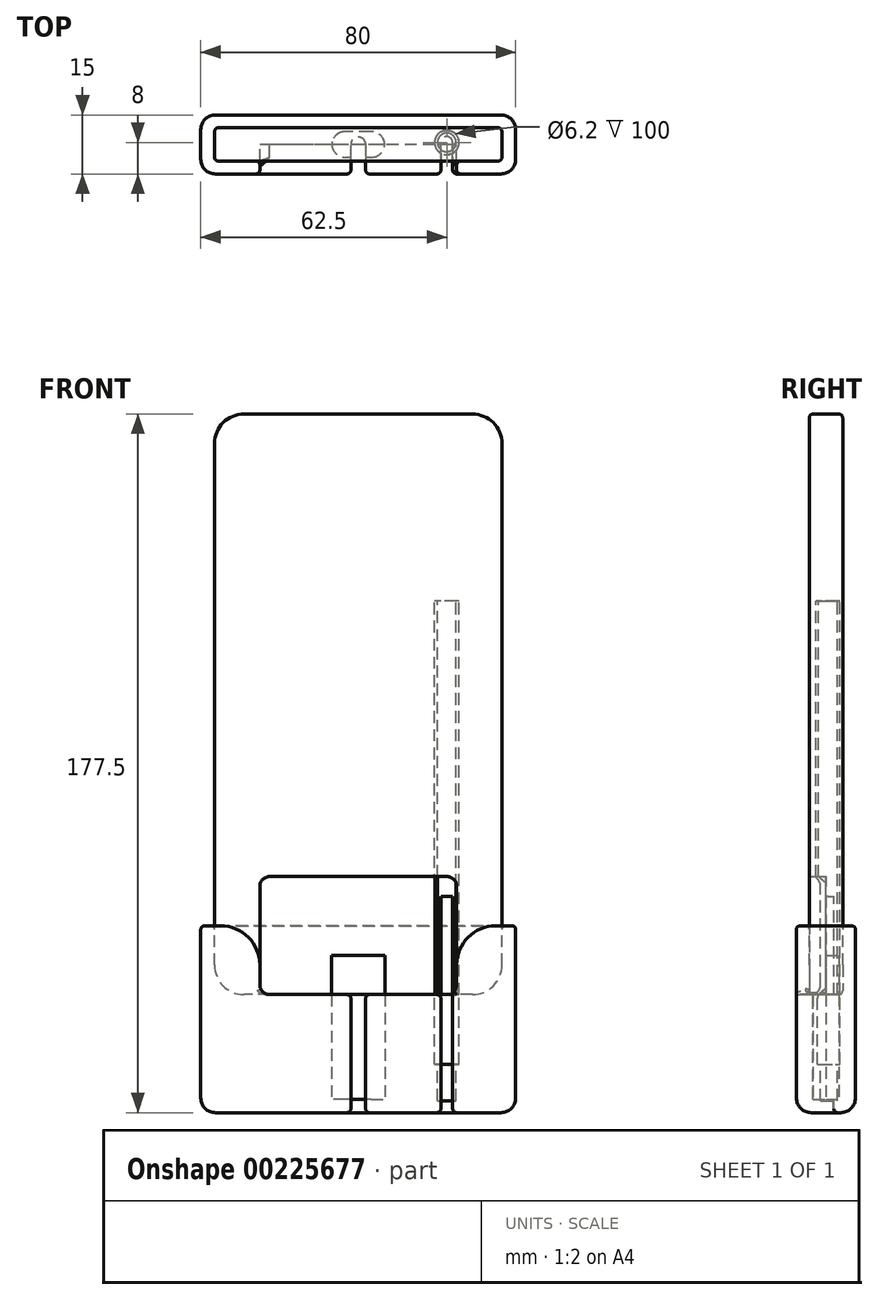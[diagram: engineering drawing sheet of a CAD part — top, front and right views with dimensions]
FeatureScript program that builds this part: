
annotation { "Feature Type Name" : "Feature", "Feature Type Description" : "" }
export const myFeature = defineFeature(function(context is Context, id is Id, definition is map)
    precondition{}
    {
        {
            var Q0;
            Q0=qCreatedBy(makeId("Front.planeOp"),FACE);
            var sketch = newSketch(context, id + "F0", { "sketchPlane" : qUnion([Q0])});
            skLineSegment(sketch, "E0.bottom", {"start": v(29, 0) * mm, "end": v(-29, 0) * mm});
            skLineSegment(sketch, "E0.top", {"start": v(29, 147.5) * mm, "end": v(-29, 147.5) * mm});
            skLineSegment(sketch, "E0.left", {"start": v(36.5, 7.5) * mm, "end": v(36.5, 140) * mm});
            skLineSegment(sketch, "E0.right", {"start": v(-36.5, 7.5) * mm, "end": v(-36.5, 140) * mm});
            skPoint(sketch, "E1.visualSharp", {"position": v(36.5, 147.5) * mm});
            skArc(sketch, "E1.filletArc", {"start": v(36.5, 140) * mm, "mid": v(34.3, 145.3) * mm, "end": v(29, 147.5) * mm});
            skPoint(sketch, "E2.visualSharp", {"position": v(-36.5, 147.5) * mm});
            skArc(sketch, "E2.filletArc", {"start": v(-29, 147.5) * mm, "mid": v(-34.3, 145.3) * mm, "end": v(-36.5, 140) * mm});
            skPoint(sketch, "E3.visualSharp", {"position": v(36.5, 0) * mm});
            skArc(sketch, "E3.filletArc", {"start": v(29, 0) * mm, "mid": v(34.3, 2.2) * mm, "end": v(36.5, 7.5) * mm});
            skPoint(sketch, "E4.visualSharp", {"position": v(-36.5, 0) * mm});
            skArc(sketch, "E4.filletArc", {"start": v(-36.5, 7.5) * mm, "mid": v(-34.3, 2.2) * mm, "end": v(-29, 0) * mm});
            skSolve(sketch);
        }
        {
            var Q0;
            Q0=makeQuery(id+"F0.imprint","IMPRINT",FACE,{"disambiguationData":[TD([[makeQuery(id+"F0.imprint","IMPRINT",EDGE,{"derivedFrom":sQuery(id+"F0.wireOp",EDGE,"E0.bottom")}),-1.0]])]});
            extrude(context, id + "F1", {"entities" : qUnion([Q0]), "endBound" : BoundingType.SYMMETRIC, "depth" : 8.5 * mm});
        }
        {
            var Q0;
            Q0=makeQuery(id+"F1.opExtrude","CAP_FACE",FACE,{"disambiguationData":[OSD([sQuery(id+"F0.wireOp",EDGE,"E0.bottom"),sQuery(id+"F0.wireOp",EDGE,"E0.top"),sQuery(id+"F0.wireOp",EDGE,"E0.left"),sQuery(id+"F0.wireOp",EDGE,"E0.right"),sQuery(id+"F0.wireOp",EDGE,"E1.filletArc"),sQuery(id+"F0.wireOp",EDGE,"E2.filletArc"),sQuery(id+"F0.wireOp",EDGE,"E3.filletArc"),sQuery(id+"F0.wireOp",EDGE,"E4.filletArc")])],"isStart":false});
            var Q1;
            Q1=makeQuery(id+"F1.opExtrude","CAP_FACE",FACE,{"disambiguationData":[OSD([sQuery(id+"F0.wireOp",EDGE,"E0.bottom"),sQuery(id+"F0.wireOp",EDGE,"E0.top"),sQuery(id+"F0.wireOp",EDGE,"E0.left"),sQuery(id+"F0.wireOp",EDGE,"E0.right"),sQuery(id+"F0.wireOp",EDGE,"E1.filletArc"),sQuery(id+"F0.wireOp",EDGE,"E2.filletArc"),sQuery(id+"F0.wireOp",EDGE,"E3.filletArc"),sQuery(id+"F0.wireOp",EDGE,"E4.filletArc")])],"isStart":true});
            fillet(context, id + "F2", {"entities" : qUnion([Q0, Q1]), "radius" : 1 * mm, "tangentPropagation" : true, "allowEdgeOverflow" : false});
        }
        {
            var Q0;
            Q0=qCreatedBy(makeId("Top.planeOp"),FACE);
            var sketch = newSketch(context, id + "F3", { "sketchPlane" : qUnion([Q0])});
            skLineSegment(sketch, "E5.bottom", {"start": v(36.25, -7.5) * mm, "end": v(-36.25, -7.5) * mm});
            skLineSegment(sketch, "E5.top", {"start": v(36.25, 7.5) * mm, "end": v(-36.25, 7.5) * mm});
            skLineSegment(sketch, "E5.left", {"start": v(40, -3.75) * mm, "end": v(40, 3.75) * mm});
            skLineSegment(sketch, "E5.right", {"start": v(-40, -3.75) * mm, "end": v(-40, 3.75) * mm});
            skPoint(sketch, "E5.middle", {"position": v(0, 0) * mm});
            skPoint(sketch, "E6.visualSharp", {"position": v(-40, 7.5) * mm});
            skArc(sketch, "E6.filletArc", {"start": v(-36.25, 7.5) * mm, "mid": v(-38.9, 6.4) * mm, "end": v(-40, 3.75) * mm});
            skPoint(sketch, "E7.visualSharp", {"position": v(-40, -7.5) * mm});
            skArc(sketch, "E7.filletArc", {"start": v(-40, -3.75) * mm, "mid": v(-38.9, -6.4) * mm, "end": v(-36.25, -7.5) * mm});
            skPoint(sketch, "E8.visualSharp", {"position": v(40, 7.5) * mm});
            skArc(sketch, "E8.filletArc", {"start": v(40, 3.75) * mm, "mid": v(38.9, 6.4) * mm, "end": v(36.25, 7.5) * mm});
            skPoint(sketch, "E9.visualSharp", {"position": v(40, -7.5) * mm});
            skArc(sketch, "E9.filletArc", {"start": v(36.25, -7.5) * mm, "mid": v(38.9, -6.4) * mm, "end": v(40, -3.75) * mm});
            skSolve(sketch);
        }
        {
            var Q0;
            Q0=makeQuery(id+"F3.imprint","IMPRINT",FACE,{"disambiguationData":[TD([[makeQuery(id+"F3.imprint","IMPRINT",EDGE,{"derivedFrom":sQuery(id+"F3.wireOp",EDGE,"E5.top")}),1.0]])]});
            extrude(context, id + "F4", {"entities" : qUnion([Q0]), "depth" : 17.5 * mm, "hasSecondDirection" : true, "secondDirectionOppositeDirection" : true, "secondDirectionDepth" : 30 * mm});
        }
        {
            var Q0;
            Q0=makeQuery(id+"F1.opExtrude","SWEPT_BODY",BODY,{"disambiguationData":[OSD([sQuery(id+"F0.wireOp",EDGE,"E0.bottom"),sQuery(id+"F0.wireOp",EDGE,"E0.top"),sQuery(id+"F0.wireOp",EDGE,"E0.left"),sQuery(id+"F0.wireOp",EDGE,"E0.right"),sQuery(id+"F0.wireOp",EDGE,"E1.filletArc"),sQuery(id+"F0.wireOp",EDGE,"E2.filletArc"),sQuery(id+"F0.wireOp",EDGE,"E3.filletArc"),sQuery(id+"F0.wireOp",EDGE,"E4.filletArc")])]});
            var Q1;
            Q1=makeQuery(id+"F4.opExtrude","SWEPT_BODY",BODY,{"disambiguationData":[OSD([sQuery(id+"F3.wireOp",EDGE,"E5.bottom"),sQuery(id+"F3.wireOp",EDGE,"E5.top"),sQuery(id+"F3.wireOp",EDGE,"E5.left"),sQuery(id+"F3.wireOp",EDGE,"E5.right"),sQuery(id+"F3.wireOp",EDGE,"E6.filletArc"),sQuery(id+"F3.wireOp",EDGE,"E7.filletArc"),sQuery(id+"F3.wireOp",EDGE,"E8.filletArc"),sQuery(id+"F3.wireOp",EDGE,"E9.filletArc"),sQuery(id+"F3.wireOp",EDGE,"vBs35ESq-FCUR-WeF2-m4bO-XcCFheQLkn9I.top"),sQuery(id+"F3.wireOp",EDGE,"vBs35ESq-FCUR-WeF2-m4bO-XcCFheQLkn9I.left"),sQuery(id+"F3.wireOp",EDGE,"vBs35ESq-FCUR-WeF2-m4bO-XcCFheQLkn9I.right"),sQuery(id+"F3.wireOp",EDGE,"07f6c711-87d0-4f36-a91b-6b1fef475164.filletArc"),sQuery(id+"F3.wireOp",EDGE,"55db23fe-f5c4-449c-865b-72b7b4b54f44.filletArc")])]});
            booleanBodies(context, id + "F5", {"operationType" : BooleanOperationType.SUBTRACTION, "tools" : qUnion([Q0]), "targets" : qUnion([Q1]), "keepTools" : true});
        }
        {
            var Q0;
            Q0=qCreatedBy(makeId("Front.planeOp"),FACE);
            var sketch = newSketch(context, id + "F6", { "sketchPlane" : qUnion([Q0])});
            skLineSegment(sketch, "E10.0", {"start": v(36.25, 17.5) * mm, "end": v(-36.25, 17.5) * mm});
            skLineSegment(sketch, "E11.bottom", {"start": v(22.5, 0) * mm, "end": v(-22.5, 0) * mm});
            skLineSegment(sketch, "E11.top", {"start": v(22.5, 30) * mm, "end": v(-22.5, 30) * mm});
            skLineSegment(sketch, "E11.left", {"start": v(25, 2.5) * mm, "end": v(25, 27.5) * mm});
            skLineSegment(sketch, "E11.right", {"start": v(-25, 2.5) * mm, "end": v(-25, 27.5) * mm});
            skPoint(sketch, "E11.middle", {"position": v(0, 17.5) * mm});
            skPoint(sketch, "E12.visualSharp", {"position": v(-25, 30) * mm});
            skArc(sketch, "E12.filletArc", {"start": v(-22.5, 30) * mm, "mid": v(-24.27, 29.27) * mm, "end": v(-25, 27.5) * mm});
            skPoint(sketch, "E13.visualSharp", {"position": v(25, 30) * mm});
            skArc(sketch, "E13.filletArc", {"start": v(25, 27.5) * mm, "mid": v(24.27, 29.27) * mm, "end": v(22.5, 30) * mm});
            skPoint(sketch, "E14.visualSharp", {"position": v(25, 0) * mm});
            skArc(sketch, "E14.filletArc", {"start": v(22.5, 0) * mm, "mid": v(24.27, 0.73) * mm, "end": v(25, 2.5) * mm});
            skPoint(sketch, "E15.visualSharp", {"position": v(-25, 0) * mm});
            skArc(sketch, "E15.filletArc", {"start": v(-25, 2.5) * mm, "mid": v(-24.27, 0.73) * mm, "end": v(-22.5, 0) * mm});
            skSolve(sketch);
        }
        {
            var Q0;
            Q0=makeQuery(id+"F6.imprint","IMPRINT",FACE,{"disambiguationData":[TD([[makeQuery(id+"F6.imprint","IMPRINT",EDGE,{"derivedFrom":sQuery(id+"F6.wireOp",EDGE,"E11.bottom")}),-1.0]])]});
            var Q1;
            Q1=makeQuery(id+"F6.imprint","IMPRINT",FACE,{"disambiguationData":[TD([[makeQuery(id+"F6.imprint","IMPRINT",EDGE,{"derivedFrom":sQuery(id+"F6.wireOp",EDGE,"E11.top")}),1.0]])]});
            extrude(context, id + "F7", {"entities" : qUnion([Q0, Q1]), "operationType" : NewBodyOperationType.REMOVE, "depth" : 25 * mm});
        }
        {
            var Q0;
            Q0=makeQuery(id+"F7.boolean.opBoolean","INTERSECT",EDGE,{"derivedFrom":[makeQuery(id+"F4.opExtrude","CAP_FACE",FACE,{"disambiguationData":[OSD([sQuery(id+"F3.wireOp",EDGE,"E5.bottom"),sQuery(id+"F3.wireOp",EDGE,"E5.top"),sQuery(id+"F3.wireOp",EDGE,"E5.left"),sQuery(id+"F3.wireOp",EDGE,"E5.right"),sQuery(id+"F3.wireOp",EDGE,"E6.filletArc"),sQuery(id+"F3.wireOp",EDGE,"E7.filletArc"),sQuery(id+"F3.wireOp",EDGE,"E8.filletArc"),sQuery(id+"F3.wireOp",EDGE,"E9.filletArc")])],"isStart":false}),makeQuery(id+"F7.opExtrude","SWEPT_FACE",FACE,{"disambiguationData":[OSD([sQuery(id+"F6.wireOp",EDGE,"E11.right")])]})]});
            var Q1;
            Q1=makeQuery(id+"F7.boolean.opBoolean","INTERSECT",EDGE,{"derivedFrom":[makeQuery(id+"F4.opExtrude","CAP_FACE",FACE,{"disambiguationData":[OSD([sQuery(id+"F3.wireOp",EDGE,"E5.bottom"),sQuery(id+"F3.wireOp",EDGE,"E5.top"),sQuery(id+"F3.wireOp",EDGE,"E5.left"),sQuery(id+"F3.wireOp",EDGE,"E5.right"),sQuery(id+"F3.wireOp",EDGE,"E6.filletArc"),sQuery(id+"F3.wireOp",EDGE,"E7.filletArc"),sQuery(id+"F3.wireOp",EDGE,"E8.filletArc"),sQuery(id+"F3.wireOp",EDGE,"E9.filletArc")])],"isStart":false}),makeQuery(id+"F7.opExtrude","SWEPT_FACE",FACE,{"disambiguationData":[OSD([sQuery(id+"F6.wireOp",EDGE,"E11.left")])]})]});
            fillet(context, id + "F8", {"entities" : qUnion([Q0, Q1]), "radius" : 10 * mm, "tangentPropagation" : true, "allowEdgeOverflow" : false});
        }
        {
            var Q0;
            Q0=makeQuery(id+"F4.opExtrude","CAP_EDGE",EDGE,{"disambiguationData":[OSD([sQuery(id+"F3.wireOp",EDGE,"E5.left")])],"isStart":true});
            fillet(context, id + "F9", {"entities" : qUnion([Q0]), "radius" : 3.75 * mm, "tangentPropagation" : true, "allowEdgeOverflow" : false});
        }
        {
            var Q0;
            Q0=makeQuery(id+"F4.opExtrude","CAP_EDGE",EDGE,{"disambiguationData":[OSD([sQuery(id+"F3.wireOp",EDGE,"E5.top")])],"isStart":false});
            var Q1;
            Q1=makeQuery(id+"F5.opBoolean","INTERSECT",EDGE,{"derivedFrom":[makeQuery(id+"F1.opExtrude","CAP_FACE",FACE,{"disambiguationData":[OSD([sQuery(id+"F0.wireOp",EDGE,"E0.bottom"),sQuery(id+"F0.wireOp",EDGE,"E0.top"),sQuery(id+"F0.wireOp",EDGE,"E0.left"),sQuery(id+"F0.wireOp",EDGE,"E0.right"),sQuery(id+"F0.wireOp",EDGE,"E1.filletArc"),sQuery(id+"F0.wireOp",EDGE,"E2.filletArc"),sQuery(id+"F0.wireOp",EDGE,"E3.filletArc"),sQuery(id+"F0.wireOp",EDGE,"E4.filletArc")])],"isStart":true}),makeQuery(id+"F4.opExtrude","CAP_FACE",FACE,{"disambiguationData":[OSD([sQuery(id+"F3.wireOp",EDGE,"E5.bottom"),sQuery(id+"F3.wireOp",EDGE,"E5.top"),sQuery(id+"F3.wireOp",EDGE,"E5.left"),sQuery(id+"F3.wireOp",EDGE,"E5.right"),sQuery(id+"F3.wireOp",EDGE,"E6.filletArc"),sQuery(id+"F3.wireOp",EDGE,"E7.filletArc"),sQuery(id+"F3.wireOp",EDGE,"E8.filletArc"),sQuery(id+"F3.wireOp",EDGE,"E9.filletArc")])],"isStart":false})]});
            fillet(context, id + "F10", {"entities" : qUnion([Q0, Q1]), "radius" : 1 * mm, "tangentPropagation" : true, "allowEdgeOverflow" : false});
        }
        {
            var Q0;
            Q0=qCreatedBy(makeId("Top.planeOp"),FACE);
            var sketch = newSketch(context, id + "F11", { "sketchPlane" : qUnion([Q0])});
            skLineSegment(sketch, "E16.bottom", {"start": v(3.25, -3.3) * mm, "end": v(-3.25, -3.3) * mm});
            skLineSegment(sketch, "E16.top", {"start": v(3.25, 3.3) * mm, "end": v(-3.25, 3.3) * mm});
            skLineSegment(sketch, "E16.left", {"start": v(6.75, -0.2) * mm, "end": v(6.75, 0.2) * mm});
            skLineSegment(sketch, "E16.right", {"start": v(-6.75, -0.2) * mm, "end": v(-6.75, 0.2) * mm});
            skPoint(sketch, "E16.middle", {"position": v(0, 0) * mm});
            skPoint(sketch, "E17.visualSharp", {"position": v(-6.75, 3.3) * mm});
            skArc(sketch, "E17.filletArc", {"start": v(-3.25, 3.3) * mm, "mid": v(-5.72, 2.27) * mm, "end": v(-6.75, -0.2) * mm});
            skPoint(sketch, "E18.visualSharp", {"position": v(6.75, 3.3) * mm});
            skArc(sketch, "E18.filletArc", {"start": v(6.75, -0.2) * mm, "mid": v(5.72, 2.27) * mm, "end": v(3.25, 3.3) * mm});
            skPoint(sketch, "E19.visualSharp", {"position": v(6.75, -3.3) * mm});
            skArc(sketch, "E19.filletArc", {"start": v(3.25, -3.3) * mm, "mid": v(5.72, -2.27) * mm, "end": v(6.75, 0.2) * mm});
            skPoint(sketch, "E20.visualSharp", {"position": v(-6.75, -3.3) * mm});
            skArc(sketch, "E20.filletArc", {"start": v(-6.75, 0.2) * mm, "mid": v(-5.72, -2.27) * mm, "end": v(-3.25, -3.3) * mm});
            skSolve(sketch);
        }
        {
            var Q0;
            {var subQ7=sQuery(id+"F11.wireOp",EDGE,"E16.bottom");Q0=makeQuery(id+"F11.imprint","IMPRINT",FACE,{"disambiguationData":[TD([[makeQuery(id+"F11.imprint","IMPRINT",EDGE,{"derivedFrom":subQ7}),-1.0]])]});}
            extrude(context, id + "F12", {"entities" : qUnion([Q0]), "operationType" : NewBodyOperationType.REMOVE, "depth" : 10 * mm, "hasSecondDirection" : true, "secondDirectionOppositeDirection" : true, "secondDirectionDepth" : 26.6 * mm});
        }
        {
            var Q0;
            Q0=qCreatedBy(makeId("Top.planeOp"),FACE);
            var sketch = newSketch(context, id + "F13", { "sketchPlane" : qUnion([Q0])});
            skCircle(sketch, "E21", {"center": v(0, 0) * mm, "radius": 1.88 * mm});
            skLineSegment(sketch, "E22", {"start": v(1.88, 0) * mm, "end": v(1.88, -10) * mm});
            skLineSegment(sketch, "E23", {"start": v(1.88, -10) * mm, "end": v(-1.87, -10) * mm});
            skLineSegment(sketch, "E24", {"start": v(-1.87, -10) * mm, "end": v(-1.88, 0) * mm});
            skSolve(sketch);
        }
        {
            var Q0;
            {var subQ0=sQuery(id+"F13.wireOp",EDGE,"E21");var subQ1=makeQuery(id+"F13.imprint","INTERSECT",VERTEX,{"derivedFrom":[subQ0,sQuery(id+"F13.wireOp",EDGE,"E22")]});Q0=makeQuery(id+"F13.imprint","IMPRINT",FACE,{"disambiguationData":[TD([[makeQuery(id+"F13.imprint","IMPRINT",EDGE,{"disambiguationData":[TD([[subQ1,-1.0]])],"derivedFrom":subQ0}),1.0]])]});}
            var Q1;
            {var subQ0=sQuery(id+"F13.wireOp",EDGE,"E22");Q1=makeQuery(id+"F13.imprint","IMPRINT",FACE,{"disambiguationData":[TD([[makeQuery(id+"F13.imprint","IMPRINT",EDGE,{"derivedFrom":subQ0}),-1.0]])]});}
            extrude(context, id + "F14", {"entities" : qUnion([Q0, Q1]), "operationType" : NewBodyOperationType.REMOVE, "oppositeDirection" : true, "depth" : 30 * mm});
        }
        {
            var Q0;
            Q0=qCreatedBy(makeId("Top.planeOp"),FACE);
            var sketch = newSketch(context, id + "F15", { "sketchPlane" : qUnion([Q0])});
            skCircle(sketch, "E25", {"center": v(22.5, 0.5) * mm, "radius": 3.1 * mm});
            skCircle(sketch, "E26", {"center": v(22.5, 0.5) * mm, "radius": 2.38 * mm});
            skSolve(sketch);
        }
        {
            var Q0;
            Q0=makeQuery(id+"F15.imprint","IMPRINT",FACE,{"disambiguationData":[TD([[makeQuery(id+"F15.imprint","IMPRINT",EDGE,{"derivedFrom":sQuery(id+"F15.wireOp",EDGE,"E25")}),1.0]])]});
            extrude(context, id + "F16", {"entities" : qUnion([Q0]), "operationType" : NewBodyOperationType.REMOVE, "oppositeDirection" : true, "depth" : 17.7 * mm, "hasSecondDirection" : true, "secondDirectionOppositeDirection" : false, "secondDirectionDepth" : 100 * mm});
        }
        {
            var Q0;
            Q0=makeQuery(id+"F15.imprint","IMPRINT",FACE,{"disambiguationData":[TD([[makeQuery(id+"F15.imprint","IMPRINT",EDGE,{"derivedFrom":sQuery(id+"F15.wireOp",EDGE,"E26")}),1.0]])]});
            extrude(context, id + "F17", {"entities" : qUnion([Q0]), "operationType" : NewBodyOperationType.REMOVE, "oppositeDirection" : true, "depth" : 27 * mm});
        }
        {
            var Q0;
            Q0=qCreatedBy(makeId("Top.planeOp"),FACE);
            var sketch = newSketch(context, id + "F18", { "sketchPlane" : qUnion([Q0])});
            skPoint(sketch, "E27.0", {"position": v(22.5, 0.5) * mm});
            skCircle(sketch, "E28", {"center": v(22.5, 0.5) * mm, "radius": 1.5 * mm});
            skLineSegment(sketch, "E29", {"start": v(24, 0.5) * mm, "end": v(24, -10) * mm});
            skLineSegment(sketch, "E30", {"start": v(24, -10) * mm, "end": v(21, -10) * mm});
            skLineSegment(sketch, "E31", {"start": v(21, -10) * mm, "end": v(21, 0.5) * mm});
            skSolve(sketch);
        }
        {
            var Q0;
            {var subQ0=sQuery(id+"F18.wireOp",EDGE,"E28");var subQ1=makeQuery(id+"F18.imprint","INTERSECT",VERTEX,{"derivedFrom":[subQ0,sQuery(id+"F18.wireOp",EDGE,"E29")]});Q0=makeQuery(id+"F18.imprint","IMPRINT",FACE,{"disambiguationData":[TD([[makeQuery(id+"F18.imprint","IMPRINT",EDGE,{"disambiguationData":[TD([[subQ1,-1.0]])],"derivedFrom":subQ0}),1.0]])]});}
            var Q1;
            {var subQ0=sQuery(id+"F18.wireOp",EDGE,"E29");Q1=makeQuery(id+"F18.imprint","IMPRINT",FACE,{"disambiguationData":[TD([[makeQuery(id+"F18.imprint","IMPRINT",EDGE,{"derivedFrom":subQ0}),-1.0]])]});}
            extrude(context, id + "F19", {"entities" : qUnion([Q0, Q1]), "operationType" : NewBodyOperationType.REMOVE, "oppositeDirection" : true, "depth" : 30 * mm, "hasSecondDirection" : true, "secondDirectionOppositeDirection" : false, "secondDirectionDepth" : 25 * mm});
        }
        {
            var Q0;
            Q0=makeQuery(id+"F14.boolean.opBoolean","INTERSECT",EDGE,{"derivedFrom":[makeQuery(id+"F4.opExtrude","SWEPT_FACE",FACE,{"disambiguationData":[OSD([sQuery(id+"F3.wireOp",EDGE,"E5.bottom")])]}),makeQuery(id+"F14.opExtrude","SWEPT_FACE",FACE,{"disambiguationData":[OSD([sQuery(id+"F13.wireOp",EDGE,"E24")])]})]});
            var Q1;
            Q1=makeQuery(id+"F14.boolean.opBoolean","INTERSECT",EDGE,{"derivedFrom":[makeQuery(id+"F4.opExtrude","SWEPT_FACE",FACE,{"disambiguationData":[OSD([sQuery(id+"F3.wireOp",EDGE,"E5.bottom")])]}),makeQuery(id+"F14.opExtrude","SWEPT_FACE",FACE,{"disambiguationData":[OSD([sQuery(id+"F13.wireOp",EDGE,"E22")])]})]});
            var Q2;
            {var subQ0=sQuery(id+"F3.wireOp",EDGE,"E9.filletArc");var subQ7=sQuery(id+"F3.wireOp",EDGE,"E5.bottom");Q2=makeQuery(id+"F19.boolean.opBoolean","INTERSECT",EDGE,{"derivedFrom":[makeQuery(id+"F14.boolean.opBoolean","SPLIT",FACE,{"disambiguationData":[TD([makeQuery(id+"F4.opExtrude","SWEPT_FACE",FACE,{"disambiguationData":[OSD([subQ0])]})])],"derivedFrom":makeQuery(id+"F4.opExtrude","SWEPT_FACE",FACE,{"disambiguationData":[OSD([subQ7])]})}),makeQuery(id+"F19.opExtrude","SWEPT_FACE",FACE,{"disambiguationData":[OSD([sQuery(id+"F18.wireOp",EDGE,"E31")])]})]});}
            var Q3;
            {var subQ0=sQuery(id+"F3.wireOp",EDGE,"E9.filletArc");var subQ7=sQuery(id+"F3.wireOp",EDGE,"E5.bottom");Q3=makeQuery(id+"F19.boolean.opBoolean","INTERSECT",EDGE,{"derivedFrom":[makeQuery(id+"F14.boolean.opBoolean","SPLIT",FACE,{"disambiguationData":[TD([makeQuery(id+"F4.opExtrude","SWEPT_FACE",FACE,{"disambiguationData":[OSD([subQ0])]})])],"derivedFrom":makeQuery(id+"F4.opExtrude","SWEPT_FACE",FACE,{"disambiguationData":[OSD([subQ7])]})}),makeQuery(id+"F19.opExtrude","SWEPT_FACE",FACE,{"disambiguationData":[OSD([sQuery(id+"F18.wireOp",EDGE,"E29")])]})]});}
            fillet(context, id + "F20", {"entities" : qUnion([Q0, Q1, Q2, Q3]), "radius" : 1 * mm, "tangentPropagation" : true, "allowEdgeOverflow" : false});
        }
    });
